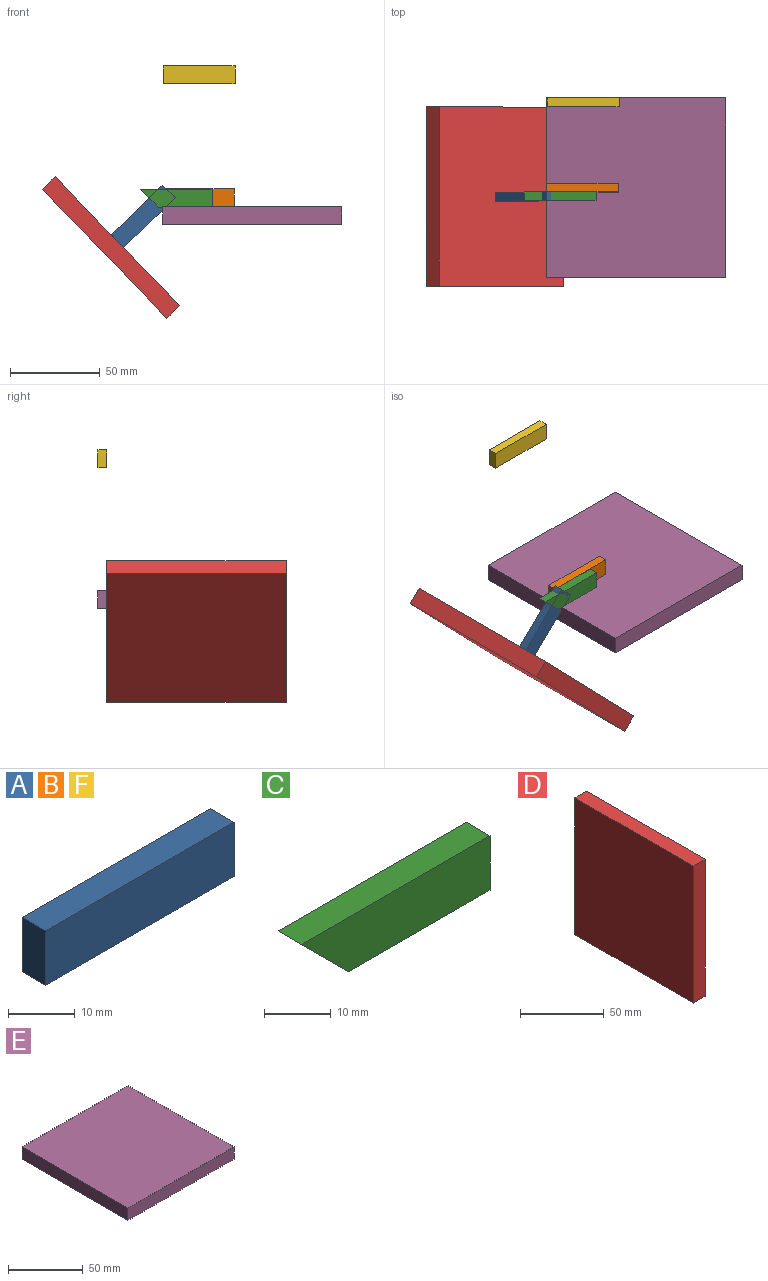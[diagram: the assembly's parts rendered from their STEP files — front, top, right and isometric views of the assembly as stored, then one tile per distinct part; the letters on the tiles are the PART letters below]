
ASSEMBLY  parts=6 mates=4
PART A: 6 faces, bbox 40x5x10 mm
  f0: plane 10x5mm, normal (1,0,0), area 50mm2, adj f1,f3,f4,f5
  f1: plane 40x5mm, normal (0,0,1), area 200mm2, adj f0,f2,f4,f5
  f2: plane 10x5mm, normal (-1,0,0), area 50mm2, adj f1,f3,f4,f5
  f3: plane 40x5mm, normal (0,0,-1), area 200mm2, adj f0,f2,f4,f5
  f4: plane 40x10mm, normal (0,-1,0), area 400mm2, adj f0,f1,f2,f3
  f5: plane 40x10mm, normal (0,1,0), area 400mm2, adj f0,f1,f2,f3
PART B: same geometry as A
PART C: 6 faces, bbox 40x5x10 mm
  f0: plane 10x5mm, normal (1,0,0), area 50mm2, adj f1,f3,f4,f5
  f1: plane 40x5mm, normal (0,0,1), area 200mm2, adj f0,f2,f4,f5
  f2: plane 10x10mm, normal (-0.71,0,-0.71), area 70.7mm2, adj f1,f3,f4,f5
  f3: plane 30x5mm, normal (0,0,-1), area 150mm2, adj f0,f2,f4,f5
  f4: plane 40x10mm, normal (0,-1,0), area 350mm2, adj f0,f1,f2,f3
  f5: plane 40x10mm, normal (0,1,0), area 350mm2, adj f0,f1,f2,f3
PART D: 6 faces, bbox 10x100x100 mm
  f0: plane 100x10mm, normal (0,0,1), area 1000mm2, adj f1,f3,f4,f5
  f1: plane 100x100mm, normal (-1,0,0), area 10000mm2, adj f0,f2,f4,f5
  f2: plane 100x10mm, normal (0,0,-1), area 1000mm2, adj f1,f3,f4,f5
  f3: plane 100x100mm, normal (1,0,0), area 10000mm2, adj f0,f2,f4,f5
  f4: plane 100x10mm, normal (0,-1,0), area 1000mm2, adj f0,f1,f2,f3
  f5: plane 100x10mm, normal (0,1,0), area 1000mm2, adj f0,f1,f2,f3
PART E: 6 faces, bbox 100x100x10 mm
  f0: plane 100x100mm, normal (0,0,1), area 10000mm2, adj f1,f3,f4,f5
  f1: plane 100x10mm, normal (-1,0,0), area 1000mm2, adj f0,f2,f4,f5
  f2: plane 100x100mm, normal (0,0,-1), area 10000mm2, adj f1,f3,f4,f5
  f3: plane 100x10mm, normal (1,0,0), area 1000mm2, adj f0,f2,f4,f5
  f4: plane 100x10mm, normal (0,-1,0), area 1000mm2, adj f0,f1,f2,f3
  f5: plane 100x10mm, normal (0,1,0), area 1000mm2, adj f0,f1,f2,f3
PART F: same geometry as A
PLACE A rot(axis=(-0.93,0,-0.37),180deg) t=(27.14,-57.5,65.3)mm
PLACE B t=(94.08,-47.5,-13.72)mm
PLACE C rot(axis=(0,-1,0),0deg) t=(82.21,-52.5,-29.62)mm
PLACE D rot(axis=(-0.93,0,-0.37),180deg) t=(-46.3,-105,20.82)mm
PLACE E t=(0.59,0,2.11)mm fixed
PLACE F t=(94.55,0,54.86)mm
MATE revolute C.f5 <-> B.f4  axis (0,1,0) through (0.49,-52.5,0.49)mm
MATE fastened D.f3 <-> A.f2  axis (0.72,0,0.69) through (-44.68,-55,-23.85)mm
MATE revolute A.f5 <-> C.f4  axis (0,-1,0) through (-19.51,-57.5,0.47)mm
MATE fastened B.f3 <-> E.f0  axis (0,0,-1) through (0.49,-50,-4.51)mm
